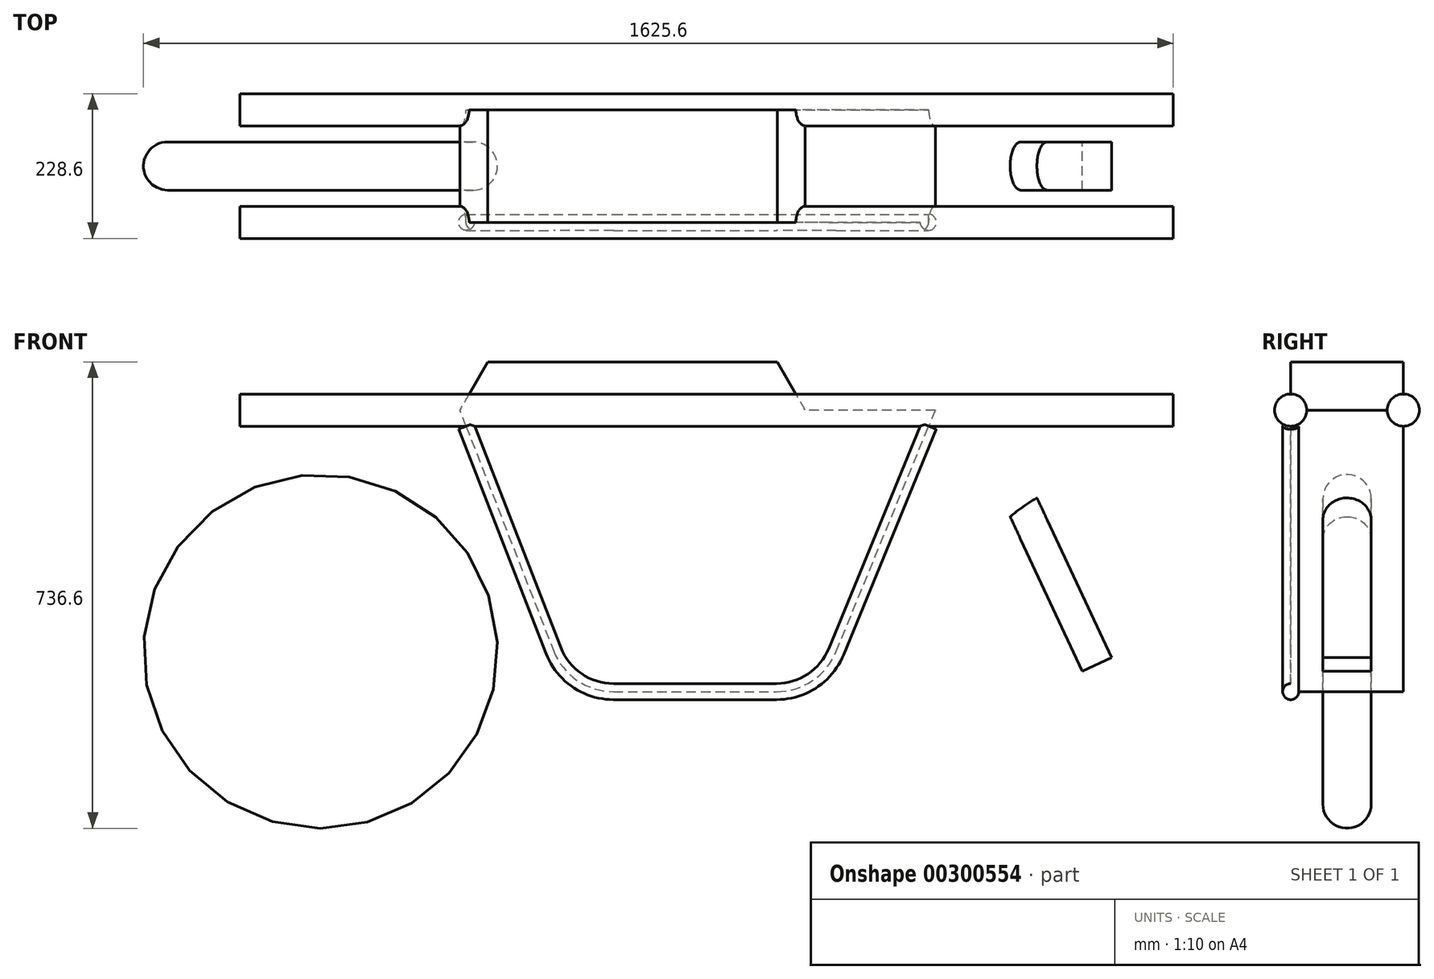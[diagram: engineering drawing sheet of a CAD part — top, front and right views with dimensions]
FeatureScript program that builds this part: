
annotation { "Feature Type Name" : "Feature", "Feature Type Description" : "" }
export const myFeature = defineFeature(function(context is Context, id is Id, definition is map)
    precondition{}
    {
        {
            var Q0;
            Q0=qCreatedBy(makeId("Front.planeOp"),FACE);
            var sketch = newSketch(context, id + "F0", { "sketchPlane" : qUnion([Q0])});
            skCircle(sketch, "E0", {"center": v(-1270, 279.4) * mm, "radius": 279.4 * mm});
            skCircle(sketch, "E1", {"center": v(0, 279.4) * mm, "radius": 279.4 * mm});
            skLineSegment(sketch, "E2", {"start": v(-1006.04, 736.6) * mm, "end": v(-548.84, 736.6) * mm});
            skLineSegment(sketch, "E3", {"start": v(-1474.76, 660.4) * mm, "end": v(146.35, 660.4) * mm});
            skLineSegment(sketch, "E4", {"start": v(-231.75, 660.4) * mm, "end": v(76.2, 0) * mm});
            skLineSegment(sketch, "E5", {"start": v(-1050.03, 660.4) * mm, "end": v(-1006.04, 736.6) * mm});
            skLineSegment(sketch, "E6", {"start": v(-876.98, 215.9) * mm, "end": v(-481.83, 215.9) * mm});
            skLineSegment(sketch, "E7", {"start": v(-548.84, 736.6) * mm, "end": v(-504.84, 660.4) * mm});
            skLineSegment(sketch, "E8", {"start": v(0, 0) * mm, "end": v(-1270, 0) * mm, "construction": true});
            skLineSegment(sketch, "E9", {"start": v(0, 279.4) * mm, "end": v(-67.45, 247.95) * mm});
            skLineSegment(sketch, "E10", {"start": v(-67.45, 247.95) * mm, "end": v(-217.73, 570.23) * mm});
            skLineSegment(sketch, "E11", {"start": v(-217.73, 570.23) * mm, "end": v(-171.69, 591.7) * mm});
            skLineSegment(sketch, "E12", {"start": v(-171.69, 591.7) * mm, "end": v(-21.4, 269.42) * mm});
            skLineSegment(sketch, "E13", {"start": v(-1050.03, 660.4) * mm, "end": v(-876.98, 215.9) * mm});
            skLineSegment(sketch, "E14", {"start": v(-481.83, 215.9) * mm, "end": v(-299.46, 660.4) * mm});
            skSolve(sketch);
        }
        {
            var Q0;
            {var subQ0=sQuery(id+"F0.wireOp",EDGE,"E5");var subQ1=sQuery(id+"F0.wireOp",EDGE,"E0");var subQ2=makeQuery(id+"F0.imprint","INTERSECT",VERTEX,{"derivedFrom":[subQ1,subQ0]});Q0=makeQuery(id+"F0.imprint","IMPRINT",FACE,{"disambiguationData":[TD([[makeQuery(id+"F0.imprint","IMPRINT",EDGE,{"disambiguationData":[TD([[subQ2,-1.0]])],"derivedFrom":subQ1}),1.0]])]});}
            var Q1;
            {var subQ0=sQuery(id+"F0.wireOp",EDGE,"E4");var subQ1=sQuery(id+"F0.wireOp",EDGE,"E1");var subQ2=makeQuery(id+"F0.imprint","INTERSECT",VERTEX,{"disambiguationData":[OD(0.0)],"derivedFrom":[subQ1,subQ0]});Q1=makeQuery(id+"F0.imprint","IMPRINT",FACE,{"disambiguationData":[TD([[makeQuery(id+"F0.imprint","IMPRINT",EDGE,{"disambiguationData":[TD([[subQ2,-1.0]])],"derivedFrom":subQ1}),1.0]])]});}
            var Q2;
            {var subQ0=sQuery(id+"F0.wireOp",EDGE,"E5");var subQ1=sQuery(id+"F0.wireOp",EDGE,"E0");var subQ2=makeQuery(id+"F0.imprint","INTERSECT",VERTEX,{"derivedFrom":[subQ1,subQ0]});Q2=makeQuery(id+"F0.imprint","IMPRINT",FACE,{"disambiguationData":[TD([[makeQuery(id+"F0.imprint","IMPRINT",EDGE,{"disambiguationData":[TD([[subQ2,1.0]])],"derivedFrom":subQ1}),1.0]])]});}
            var Q3;
            {var subQ5=sQuery(id+"F0.wireOp",EDGE,"iomXvV43-jGmP-9HCS-PqfZ-OH1Ppphl7Kk9");Q3=makeQuery(id+"F0.imprint","IMPRINT",FACE,{"disambiguationData":[TD([[makeQuery(id+"F0.imprint","IMPRINT",EDGE,{"derivedFrom":subQ5}),1.0]])]});}
            var Q4;
            {var subQ0=sQuery(id+"F0.wireOp",EDGE,"iomXvV43-jGmP-9HCS-PqfZ-OH1Ppphl7Kk9");Q4=makeQuery(id+"F0.imprint","IMPRINT",FACE,{"disambiguationData":[TD([[makeQuery(id+"F0.imprint","IMPRINT",EDGE,{"derivedFrom":subQ0}),-1.0]])]});}
            var Q5;
            {var subQ6=sQuery(id+"F0.wireOp",EDGE,"qYQvW9pK-EawE-97Le-qyWa-vBizmqQo7sgW");Q5=makeQuery(id+"F0.imprint","IMPRINT",FACE,{"disambiguationData":[TD([[makeQuery(id+"F0.imprint","IMPRINT",EDGE,{"derivedFrom":subQ6}),-1.0]])]});}
            var Q6;
            {var subQ3=sQuery(id+"F0.wireOp",EDGE,"qYQvW9pK-EawE-97Le-qyWa-vBizmqQo7sgW");Q6=makeQuery(id+"F0.imprint","IMPRINT",FACE,{"disambiguationData":[TD([[makeQuery(id+"F0.imprint","IMPRINT",EDGE,{"derivedFrom":subQ3}),1.0]])]});}
            var Q7;
            {var subQ0=sQuery(id+"F0.wireOp",EDGE,"FP18RHqU-eXeK-1vy8-IevJ-rwybb4m7QuPk");var subQ1=makeQuery(id+"F0.imprint","INTERSECT",VERTEX,{"derivedFrom":[subQ0,sQuery(id+"F0.wireOp",EDGE,"Ewv1rL4J-IIbV-51iZ-XwNo-d0kglHfARClL")]});Q7=makeQuery(id+"F0.imprint","IMPRINT",FACE,{"disambiguationData":[TD([[makeQuery(id+"F0.imprint","IMPRINT",EDGE,{"disambiguationData":[TD([[subQ1,1.0]])],"derivedFrom":subQ0}),1.0]])]});}
            var Q8;
            {var subQ0=sQuery(id+"F0.wireOp",EDGE,"E4");var subQ1=sQuery(id+"F0.wireOp",EDGE,"E1");var subQ2=makeQuery(id+"F0.imprint","INTERSECT",VERTEX,{"disambiguationData":[OD(0.0)],"derivedFrom":[subQ1,subQ0]});Q8=makeQuery(id+"F0.imprint","IMPRINT",FACE,{"disambiguationData":[TD([[makeQuery(id+"F0.imprint","IMPRINT",EDGE,{"disambiguationData":[TD([[subQ2,1.0]])],"derivedFrom":subQ1}),1.0]])]});}
            var Q9;
            {var subQ0=sQuery(id+"F0.wireOp",EDGE,"E10");var subQ1=sQuery(id+"F0.wireOp",EDGE,"E1");var subQ2=makeQuery(id+"F0.imprint","INTERSECT",VERTEX,{"derivedFrom":[subQ1,subQ0]});Q9=makeQuery(id+"F0.imprint","IMPRINT",FACE,{"disambiguationData":[TD([[makeQuery(id+"F0.imprint","IMPRINT",EDGE,{"disambiguationData":[TD([[subQ2,1.0]])],"derivedFrom":subQ1}),1.0]])]});}
            var Q10;
            {var subQ0=sQuery(id+"F0.wireOp",EDGE,"E12");var subQ1=sQuery(id+"F0.wireOp",EDGE,"E1");var subQ2=makeQuery(id+"F0.imprint","INTERSECT",VERTEX,{"derivedFrom":[subQ1,subQ0]});Q10=makeQuery(id+"F0.imprint","IMPRINT",FACE,{"disambiguationData":[TD([[makeQuery(id+"F0.imprint","IMPRINT",EDGE,{"disambiguationData":[TD([[subQ2,-1.0]])],"derivedFrom":subQ1}),1.0]])]});}
            extrude(context, id + "F1", {"entities" : qUnion([Q0, Q1, Q2, Q3, Q4, Q5, Q6, Q7, Q8, Q9, Q10]), "endBound" : BoundingType.SYMMETRIC, "offsetDistance" : 25.4 * mm, "depth" : 76.2 * mm});
        }
        {
            var Q0;
            {var subQ0=sQuery(id+"F0.wireOp",EDGE,"E13");Q0=makeQuery(id+"F0.imprint","IMPRINT",FACE,{"disambiguationData":[TD([[makeQuery(id+"F0.imprint","IMPRINT",EDGE,{"derivedFrom":subQ0}),1.0]])]});}
            var Q1;
            Q1=makeQuery(id+"F0.imprint","IMPRINT",FACE,{"disambiguationData":[TD([[makeQuery(id+"F0.imprint","IMPRINT",EDGE,{"derivedFrom":sQuery(id+"F0.wireOp",EDGE,"E2")}),-1.0]])]});
            extrude(context, id + "F2", {"entities" : qUnion([Q0, Q1]), "endBound" : BoundingType.SYMMETRIC, "depth" : 177.8 * mm, "offsetDistance" : 25.4 * mm});
        }
        {
            var Q0;
            Q0=qCreatedBy(makeId("Right.planeOp"),FACE);
            var sketch = newSketch(context, id + "F3", { "sketchPlane" : qUnion([Q0])});
            skCircle(sketch, "E15", {"center": v(-88.9, 660.4) * mm, "radius": 25.4 * mm});
            skCircle(sketch, "E16", {"center": v(88.9, 660.4) * mm, "radius": 25.4 * mm});
            skLineSegment(sketch, "E17.0", {"start": v(-88.9, 660.4) * mm, "end": v(88.9, 660.4) * mm, "construction": true});
            skSolve(sketch);
        }
        {
            var Q0;
            Q0 = qSketchRegion(id + "F3", true);
            extrude(context, id + "F4", {"entities" : qUnion([Q0]), "operationType" : NewBodyOperationType.ADD, "depth" : 76.2 * mm, "offsetDistance" : 25.4 * mm, "hasSecondDirection" : true, "secondDirectionOppositeDirection" : true, "secondDirectionDepth" : 1397 * mm});
        }
        {
            var Q0;
            Q0=makeQuery(id+"F1.opExtrude","CAP_EDGE",EDGE,{"disambiguationData":[OSD([sQuery(id+"F0.wireOp",EDGE,"E1")])],"isStart":false});
            var Q1;
            Q1=makeQuery(id+"F1.opExtrude","CAP_EDGE",EDGE,{"disambiguationData":[OSD([sQuery(id+"F0.wireOp",EDGE,"E1")])],"isStart":true});
            var Q2;
            Q2=makeQuery(id+"F1.opExtrude","CAP_EDGE",EDGE,{"disambiguationData":[OSD([sQuery(id+"F0.wireOp",EDGE,"E0")])],"isStart":false});
            var Q3;
            Q3=makeQuery(id+"F1.opExtrude","CAP_EDGE",EDGE,{"disambiguationData":[OSD([sQuery(id+"F0.wireOp",EDGE,"E0")])],"isStart":true});
            fillet(context, id + "F5", {"entities" : qUnion([Q0, Q1, Q2, Q3]), "radius" : 38.1 * mm, "tangentPropagation" : true, "allowEdgeOverflow" : false});
        }
        {
            var Q0;
            Q0=makeQuery(id+"F1.opExtrude","CAP_FACE",FACE,{"disambiguationData":[OSD([sQuery(id+"F0.wireOp",EDGE,"E1")])],"isStart":false});
            var Q1;
            {var subQ0=sQuery(id+"F0.wireOp",EDGE,"E1");Q1=makeQuery(id+"F5.opFillet","BLEND_EDGE",EDGE,{"blendedFrom":[makeQuery(id+"F1.opExtrude","CAP_EDGE",EDGE,{"disambiguationData":[OSD([subQ0])],"isStart":false}),makeQuery(id+"F1.opExtrude","CAP_FACE",FACE,{"disambiguationData":[OSD([subQ0])],"isStart":false})],"blendedInto":[makeQuery(id+"F1.opExtrude","CAP_FACE",FACE,{"disambiguationData":[OSD([subQ0])],"isStart":false})]});}
            var Q2;
            Q2=makeQuery(id+"F5.opFillet","BLEND_FACE",FACE,{"disambiguationData":[OSD([sQuery(id+"F0.wireOp",EDGE,"E1")])]});
            var Q3;
            Q3=makeQuery(id+"F1.opExtrude","CAP_FACE",FACE,{"disambiguationData":[OSD([sQuery(id+"F0.wireOp",EDGE,"E1")])],"isStart":true});
            var Q4;
            {var subQ0=sQuery(id+"F0.wireOp",EDGE,"E1");Q4=makeQuery(id+"F5.opFillet","BLEND_EDGE",EDGE,{"blendedFrom":[makeQuery(id+"F1.opExtrude","CAP_EDGE",EDGE,{"disambiguationData":[OSD([subQ0])],"isStart":true}),makeQuery(id+"F1.opExtrude","CAP_FACE",FACE,{"disambiguationData":[OSD([subQ0])],"isStart":true})],"blendedInto":[makeQuery(id+"F1.opExtrude","CAP_FACE",FACE,{"disambiguationData":[OSD([subQ0])],"isStart":true})]});}
            var Q5;
            Q5=makeQuery(id+"F2.opExtrude","SWEPT_EDGE",EDGE,{"disambiguationData":[OSD([sQuery(id+"F0.wireOp",EDGE,"E6"),sQuery(id+"F0.wireOp",EDGE,"E14")])]});
            var Q6;
            Q6=makeQuery(id+"F2.opExtrude","SWEPT_EDGE",EDGE,{"disambiguationData":[OSD([sQuery(id+"F0.wireOp",EDGE,"E6"),sQuery(id+"F0.wireOp",EDGE,"E13")])]});
            fillet(context, id + "F6", {"entities" : qUnion([Q0, Q1, Q2, Q3, Q4, Q5, Q6]), "radius" : 101.6 * mm, "tangentPropagation" : true, "allowEdgeOverflow" : false});
        }
        {
            var Q0;
            Q0=qCreatedBy(makeId("Right.planeOp"),FACE);
            cPlane(context, id + "F7", {"entities" : qUnion([Q0]), "cplaneType" : CPlaneType.OFFSET, "offset" : 635 * mm, "oppositeDirection" : true, "width" : 152.4 * mm, "height" : 152.4 * mm});
        }
        {
            var Q0;
            Q0=qCreatedBy(id+"F7.planeOp",FACE);
            var sketch = newSketch(context, id + "F8", { "sketchPlane" : qUnion([Q0])});
            skLineSegment(sketch, "E18.0", {"start": v(-88.9, 280.64) * mm, "end": v(-88.9, 215.9) * mm, "construction": true});
            skCircle(sketch, "E19", {"center": v(-88.9, 215.9) * mm, "radius": 12.7 * mm});
            skSolve(sketch);
        }
        {
            var Q0;
            Q0=makeQuery(id+"F8.imprint","IMPRINT",FACE,{"disambiguationData":[TD([[makeQuery(id+"F8.imprint","IMPRINT",EDGE,{"derivedFrom":sQuery(id+"F8.wireOp",EDGE,"E19")}),1.0]])]});
            var Q1;
            Q1=makeQuery(id+"F2.opExtrude","CAP_EDGE",EDGE,{"disambiguationData":[OSD([sQuery(id+"F0.wireOp",EDGE,"E6")])],"isStart":false});
            var Q2;
            {var subQ0=sQuery(id+"F0.wireOp",EDGE,"E6");var subQ1=sQuery(id+"F0.wireOp",EDGE,"E13");var subQ2=sQuery(id+"F0.wireOp",EDGE,"E14");Q2=makeQuery(id+"F6.opFillet","BLEND_EDGE",EDGE,{"blendedFrom":[makeQuery(id+"F2.opExtrude","SWEPT_EDGE",EDGE,{"disambiguationData":[OSD([subQ0,subQ2])]}),makeQuery(id+"F4.boolean.opBoolean","SPLIT",FACE,{"disambiguationData":[TD([makeQuery(id+"F2.opExtrude","SWEPT_FACE",FACE,{"disambiguationData":[OSD([subQ0])]})])],"derivedFrom":makeQuery(id+"F2.opExtrude","CAP_FACE",FACE,{"disambiguationData":[OSD([sQuery(id+"F0.wireOp",EDGE,"E2"),sQuery(id+"F0.wireOp",EDGE,"E3"),sQuery(id+"F0.wireOp",EDGE,"E5"),subQ0,sQuery(id+"F0.wireOp",EDGE,"E7"),subQ1,subQ2])],"isStart":false})})],"blendedInto":[makeQuery(id+"F4.boolean.opBoolean","SPLIT",FACE,{"disambiguationData":[TD([makeQuery(id+"F2.opExtrude","SWEPT_FACE",FACE,{"disambiguationData":[OSD([subQ0])]})])],"derivedFrom":makeQuery(id+"F2.opExtrude","CAP_FACE",FACE,{"disambiguationData":[OSD([sQuery(id+"F0.wireOp",EDGE,"E2"),sQuery(id+"F0.wireOp",EDGE,"E3"),sQuery(id+"F0.wireOp",EDGE,"E5"),subQ0,sQuery(id+"F0.wireOp",EDGE,"E7"),subQ1,subQ2])],"isStart":false})})]});}
            var Q3;
            Q3=makeQuery(id+"F2.opExtrude","CAP_EDGE",EDGE,{"disambiguationData":[OSD([sQuery(id+"F0.wireOp",EDGE,"E14")])],"isStart":false});
            var Q4;
            {var subQ0=sQuery(id+"F0.wireOp",EDGE,"E6");var subQ1=sQuery(id+"F0.wireOp",EDGE,"E13");var subQ2=sQuery(id+"F0.wireOp",EDGE,"E14");Q4=makeQuery(id+"F6.opFillet","BLEND_EDGE",EDGE,{"blendedFrom":[makeQuery(id+"F2.opExtrude","SWEPT_EDGE",EDGE,{"disambiguationData":[OSD([subQ0,subQ1])]}),makeQuery(id+"F4.boolean.opBoolean","SPLIT",FACE,{"disambiguationData":[TD([makeQuery(id+"F2.opExtrude","SWEPT_FACE",FACE,{"disambiguationData":[OSD([subQ0])]})])],"derivedFrom":makeQuery(id+"F2.opExtrude","CAP_FACE",FACE,{"disambiguationData":[OSD([sQuery(id+"F0.wireOp",EDGE,"E2"),sQuery(id+"F0.wireOp",EDGE,"E3"),sQuery(id+"F0.wireOp",EDGE,"E5"),subQ0,sQuery(id+"F0.wireOp",EDGE,"E7"),subQ1,subQ2])],"isStart":false})})],"blendedInto":[makeQuery(id+"F4.boolean.opBoolean","SPLIT",FACE,{"disambiguationData":[TD([makeQuery(id+"F2.opExtrude","SWEPT_FACE",FACE,{"disambiguationData":[OSD([subQ0])]})])],"derivedFrom":makeQuery(id+"F2.opExtrude","CAP_FACE",FACE,{"disambiguationData":[OSD([sQuery(id+"F0.wireOp",EDGE,"E2"),sQuery(id+"F0.wireOp",EDGE,"E3"),sQuery(id+"F0.wireOp",EDGE,"E5"),subQ0,sQuery(id+"F0.wireOp",EDGE,"E7"),subQ1,subQ2])],"isStart":false})})]});}
            var Q5;
            Q5=makeQuery(id+"F2.opExtrude","CAP_EDGE",EDGE,{"disambiguationData":[OSD([sQuery(id+"F0.wireOp",EDGE,"E13")])],"isStart":false});
            sweep(context, id + "F9", {"operationType" : NewBodyOperationType.ADD, "profiles" : qUnion([Q0]), "path" : qUnion([Q1, Q2, Q3, Q4, Q5])});
        }
    });
